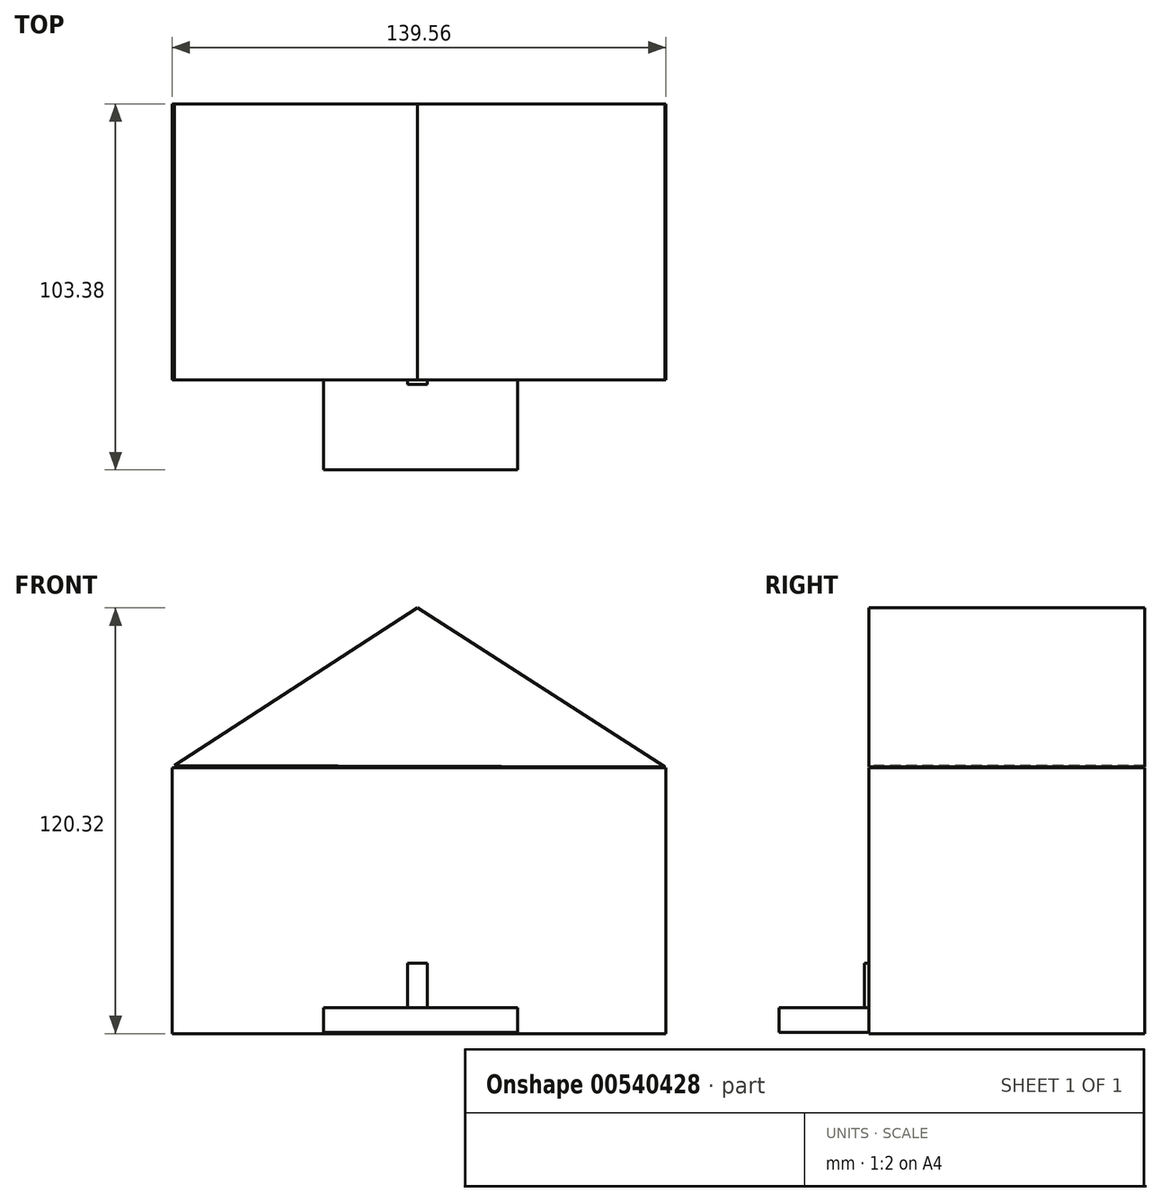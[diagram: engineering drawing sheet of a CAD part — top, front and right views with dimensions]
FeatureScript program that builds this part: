
annotation { "Feature Type Name" : "Feature", "Feature Type Description" : "" }
export const myFeature = defineFeature(function(context is Context, id is Id, definition is map)
    precondition{}
    {
        {
            var Q0;
            Q0=qCreatedBy(makeId("Front.planeOp"),FACE);
            var sketch = newSketch(context, id + "F0", { "sketchPlane" : qUnion([Q0])});
            skLineSegment(sketch, "E0.bottom", {"start": v(-69.32, 30.23) * mm, "end": v(70.24, 30.23) * mm});
            skLineSegment(sketch, "E0.top", {"start": v(-69.32, -44.9) * mm, "end": v(70.24, -44.9) * mm});
            skLineSegment(sketch, "E0.left", {"start": v(-69.32, 30.23) * mm, "end": v(-69.32, -44.9) * mm});
            skLineSegment(sketch, "E0.right", {"start": v(70.24, 30.23) * mm, "end": v(70.24, -44.9) * mm});
            skSolve(sketch);
        }
        {
            var Q0;
            Q0 = qSketchRegion(id + "F0", true);
            var Q1;
            Q1=makeQuery(id+"F0.imprint","IMPRINT",FACE,{"disambiguationData":[TD([[makeQuery(id+"F0.imprint","IMPRINT",EDGE,{"derivedFrom":sQuery(id+"F0.wireOp",EDGE,"E0.bottom")}),-1.0]])]});
            extrude(context, id + "F1", {"entities" : qUnion([Q0, Q1]), "oppositeDirection" : true, "depth" : 77.98 * mm, "offsetDistance" : 25.4 * mm});
        }
        {
            var Q0;
            Q0=qCreatedBy(makeId("Front.planeOp"),FACE);
            var sketch = newSketch(context, id + "F2", { "sketchPlane" : qUnion([Q0])});
            skLineSegment(sketch, "E1", {"start": v(-68.71, 30.84) * mm, "end": v(0, 75.43) * mm});
            skLineSegment(sketch, "E2", {"start": v(0, 75.43) * mm, "end": v(69.93, 30.54) * mm});
            skLineSegment(sketch, "E3", {"start": v(-68.71, 30.84) * mm, "end": v(69.93, 30.54) * mm});
            skSolve(sketch);
        }
        {
            var Q0;
            Q0 = qSketchRegion(id + "F2", true);
            extrude(context, id + "F3", {"entities" : qUnion([Q0]), "oppositeDirection" : true, "depth" : 77.98 * mm, "offsetDistance" : 25.4 * mm});
        }
        {
            var Q0;
            Q0=makeQuery(id+"F1.opExtrude","CAP_FACE",FACE,{"disambiguationData":[OSD([sQuery(id+"F0.wireOp",EDGE,"E0.bottom"),sQuery(id+"F0.wireOp",EDGE,"E0.top"),sQuery(id+"F0.wireOp",EDGE,"E0.left"),sQuery(id+"F0.wireOp",EDGE,"E0.right")])],"isStart":true});
            var sketch = newSketch(context, id + "F4", { "sketchPlane" : qUnion([Q0])});
            skSolve(sketch);
        }
        {
            var Q0;
            Q0=makeQuery(id+"F4.imprint","IMPRINT",FACE,{"disambiguationData":[TD([[makeQuery(id+"F4.imprint","IMPRINT",EDGE,{"derivedFrom":makeQuery(id+"F1.opExtrude","CAP_EDGE",EDGE,{"disambiguationData":[OSD([sQuery(id+"F0.wireOp",EDGE,"E0.bottom")])],"isStart":true})}),-1.0]])]});
            var sketch = newSketch(context, id + "F5", { "sketchPlane" : qUnion([Q0])});
            skLineSegment(sketch, "E4.bottom", {"start": v(-26.57, -44.59) * mm, "end": v(28.4, -44.59) * mm});
            skLineSegment(sketch, "E4.top", {"start": v(-26.57, -37.56) * mm, "end": v(28.4, -37.56) * mm});
            skLineSegment(sketch, "E4.left", {"start": v(-26.57, -44.59) * mm, "end": v(-26.57, -37.56) * mm});
            skLineSegment(sketch, "E4.right", {"start": v(28.4, -44.59) * mm, "end": v(28.4, -37.56) * mm});
            skSolve(sketch);
        }
        {
            var Q0;
            Q0 = qSketchRegion(id + "F5", true);
            extrude(context, id + "F6", {"entities" : qUnion([Q0]), "operationType" : NewBodyOperationType.ADD, "depth" : 25.4 * mm, "offsetDistance" : 25.4 * mm});
        }
        {
            var Q0;
            Q0=makeQuery(id+"F4.imprint","IMPRINT",FACE,{"disambiguationData":[TD([[makeQuery(id+"F4.imprint","IMPRINT",EDGE,{"derivedFrom":makeQuery(id+"F1.opExtrude","CAP_EDGE",EDGE,{"disambiguationData":[OSD([sQuery(id+"F0.wireOp",EDGE,"E0.bottom")])],"isStart":true})}),-1.0]])]});
            var sketch = newSketch(context, id + "F7", { "sketchPlane" : qUnion([Q0])});
            skLineSegment(sketch, "E5.bottom", {"start": v(-2.75, -38.17) * mm, "end": v(2.75, -38.17) * mm});
            skLineSegment(sketch, "E5.top", {"start": v(-2.75, -25.04) * mm, "end": v(2.75, -25.04) * mm});
            skLineSegment(sketch, "E5.left", {"start": v(-2.75, -38.17) * mm, "end": v(-2.75, -25.04) * mm});
            skLineSegment(sketch, "E5.right", {"start": v(2.75, -38.17) * mm, "end": v(2.75, -25.04) * mm});
            skSolve(sketch);
        }
        {
            var Q0;
            Q0 = qSketchRegion(id + "F7", true);
            extrude(context, id + "F8", {"entities" : qUnion([Q0]), "operationType" : NewBodyOperationType.ADD, "depth" : 1.27 * mm, "offsetDistance" : 25.4 * mm});
        }
    });
